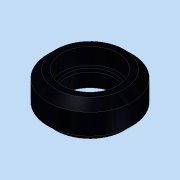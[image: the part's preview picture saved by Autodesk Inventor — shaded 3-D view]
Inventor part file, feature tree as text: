
AUTODESK INVENTOR PART (.ipt)
format: ipt  version: 2013 SP2 (Build 170200200, 200)  size: 107,520 bytes
history: native  units: mm
features: revolve x1, mirror x1, sketch x1
ambient origin geometry x8: Origin, YZ Plane, XZ Plane, XY Plane, X Axis, Y Axis, Z Axis, Center Point
bodies: Solid1 (feature_tree)
feature tree (3):
  revolve  "Revolution1"  [1 undecoded]
  mirror  "Mirror1"
  sketch  "Sketch1"  dims[d2=23.89mm d4=2.945mm d5=19.54mm d6=5.115mm d7=15.974mm d8=0.5mm d9=13.89mm d10=90.0deg]
note: 1 required parameter value undecoded (feature->parameter linkage not recoverable at this tier; creation-order binding heuristic only, values carry confidence <= 0.55)
